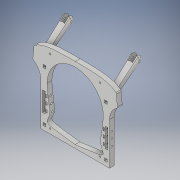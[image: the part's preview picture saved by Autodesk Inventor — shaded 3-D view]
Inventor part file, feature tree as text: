
AUTODESK INVENTOR PART (.ipt)
format: ipt  version: 2019 (Build 230136000, 136)  size: 1,089,024 bytes
history: native  units: mm
features: sketch x19, extrude x13, other x6, mirror x6, projected_geometry x5, revolve x1, loft x1, fillet x1
ambient origin geometry x8: Origin, YZ Plane, XZ Plane, XY Plane, X Axis, Y Axis, Z Axis, Center Point
bodies: Body1 (feature_tree)
feature tree (52):
  other  "Bryła1"
  extrude  "Wyciągnięcie proste1"  Depth=30.0mm
  sketch  "Szkic3"
  extrude  "Wyciągnięcie proste2"  Depth=65.0mm
  extrude  "Wyciągnięcie proste3"  Depth=9.0mm TaperAngle=0.0deg
  extrude  "Wyciągnięcie proste4"  Depth=3.0mm
  extrude  "Wyciągnięcie proste5"  Depth=3.0mm
  other  "Płaszczyzna konstrukcyjna1"
  mirror  "Odbij1"
  sketch  "Szkic7"
  extrude  "Wyciągnięcie proste6"  Depth=3.0mm
  extrude  "Wyciągnięcie proste7"  Depth=3.0mm
  extrude  "Wyciągnięcie proste8"  Depth=160.0mm
  mirror  "Odbij2"
  sketch  "Szkic9"
  other  "Płaszczyzna konstrukcyjna3"
  other  "Płaszczyzna konstrukcyjna5"
  revolve  "Obrót1"
  loft  "Wyciągnięcie złożone2"
  mirror  "Odbij3"
  extrude  "Wyciągnięcie proste9"  Depth=9.0mm TaperAngle=0.0deg
  mirror  "Odbij4"
  sketch  "Szkic14"
  extrude  "Wyciągnięcie proste10"  Depth=9.0mm TaperAngle=0.0deg
  mirror  "Odbij5"
  extrude  "Wyciągnięcie proste11"  Depth=6.0mm
  fillet  "Zaokrąglenie2"  Radius=3.0mm
  sketch  "Szkic17"
  sketch  "Szkic18"
  sketch  "Szkic19"
  sketch  "Szkic20"
  other  "Płaszczyzna konstrukcyjna6"
  extrude  "Wyciągnięcie proste12"  Depth=12.5mm
  extrude  "Wyciągnięcie proste13"  Depth=3.0mm
  mirror  "Odbij6"
  sketch  "Szkic2"
  sketch  "Szkic4"
  sketch  "Szkic5"
  sketch  "Szkic6"
  sketch  "Szkic8"
  projected_geometry  "Pętla rzutowana1"
  sketch  "Szkic12"
  other  "Krawędzie1"
  sketch  "Szkic13"
  projected_geometry  "Pętla rzutowana3"
  projected_geometry  "Pętla rzutowana4"
  sketch  "Szkic15"
  projected_geometry  "Pętla rzutowana5"
  sketch  "Szkic16"
  sketch  "Szkic21"
  sketch  "Szkic22"
  projected_geometry  "Pętla rzutowana6"
